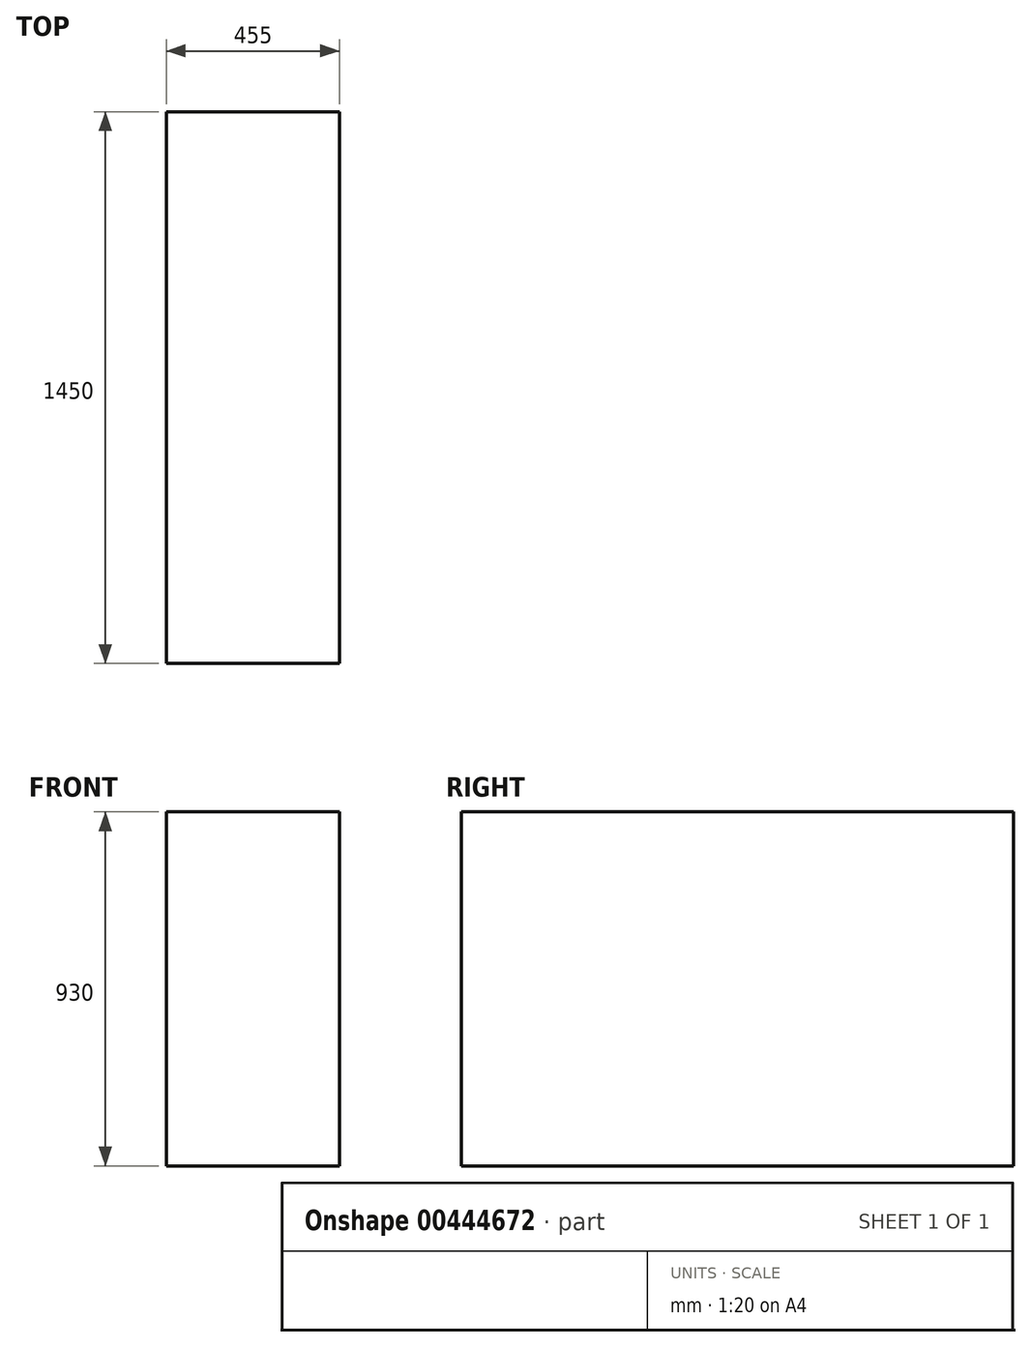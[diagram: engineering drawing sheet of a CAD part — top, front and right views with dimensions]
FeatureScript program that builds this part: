
annotation { "Feature Type Name" : "Feature", "Feature Type Description" : "" }
export const myFeature = defineFeature(function(context is Context, id is Id, definition is map)
    precondition{}
    {
        {
            var Q0;
            Q0=qCreatedBy(makeId("Top.planeOp"),FACE);
            var sketch = newSketch(context, id + "F0", { "sketchPlane" : qUnion([Q0])});
            skLineSegment(sketch, "E0.bottom", {"start": v(0, 0) * mm, "end": v(455, 0) * mm});
            skLineSegment(sketch, "E0.top", {"start": v(0, 1450) * mm, "end": v(455, 1450) * mm});
            skLineSegment(sketch, "E0.left", {"start": v(0, 0) * mm, "end": v(0, 1450) * mm});
            skLineSegment(sketch, "E0.right", {"start": v(455, 0) * mm, "end": v(455, 1450) * mm});
            skSolve(sketch);
        }
        {
            var Q0;
            Q0 = qSketchRegion(id + "F0", true);
            extrude(context, id + "F1", {"entities" : qUnion([Q0]), "depth" : 930 * mm});
        }
    });
